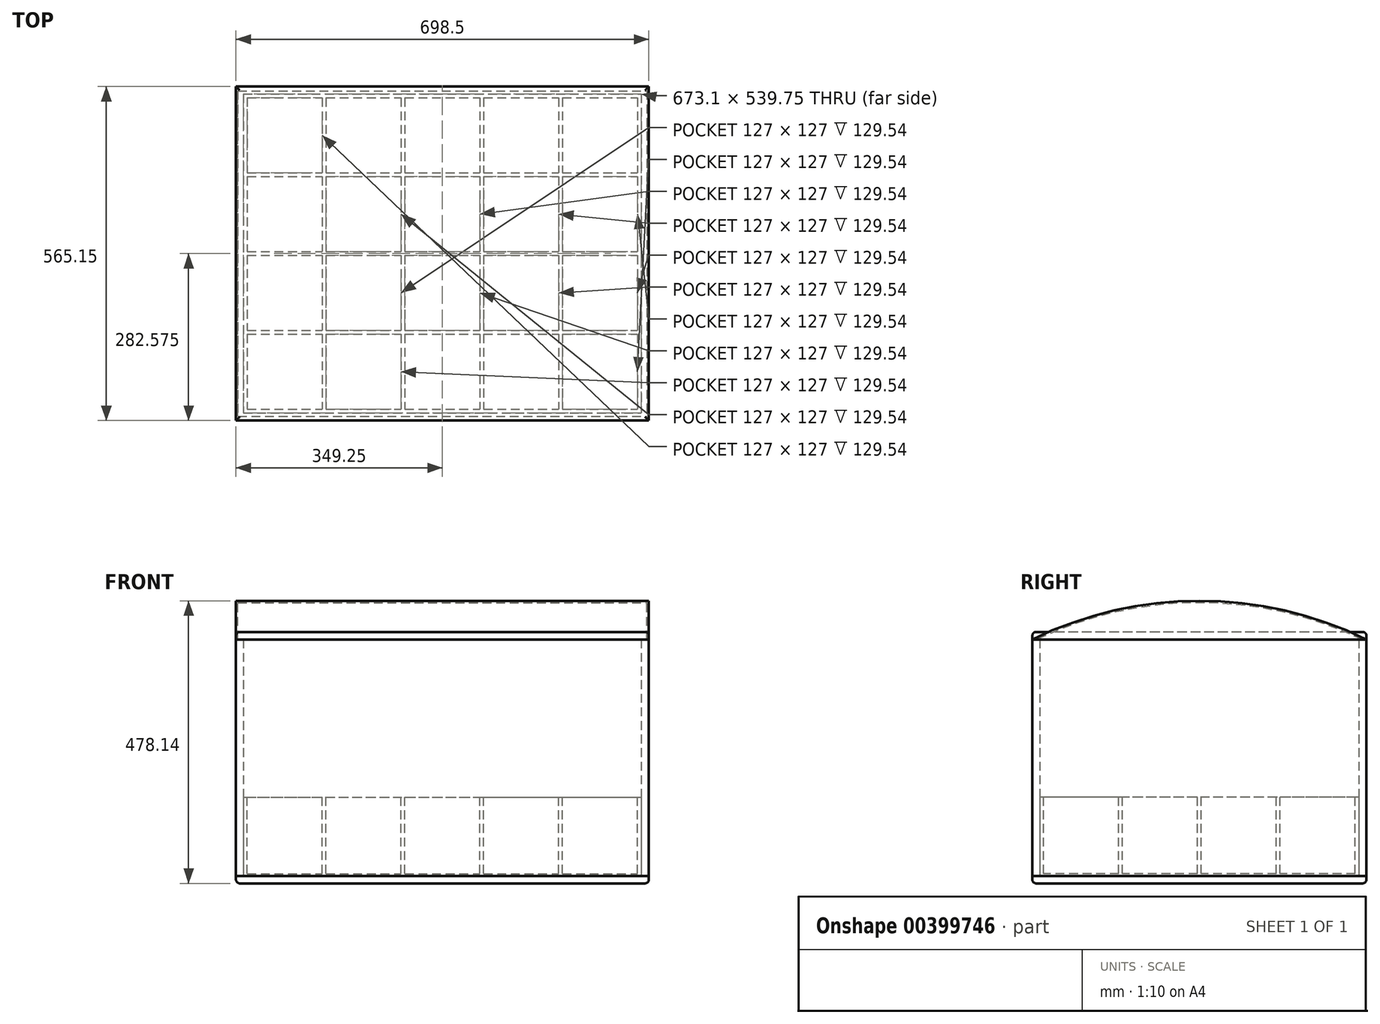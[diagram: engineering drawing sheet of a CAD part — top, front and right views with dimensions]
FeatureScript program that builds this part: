
annotation { "Feature Type Name" : "Feature", "Feature Type Description" : "" }
export const myFeature = defineFeature(function(context is Context, id is Id, definition is map)
    precondition{}
    {
        {
            var Q0;
            Q0=qCreatedBy(makeId("Top.planeOp"),FACE);
            var sketch = newSketch(context, id + "F0", { "sketchPlane" : qUnion([Q0])});
            skLineSegment(sketch, "E0.bottom", {"start": v(0, 0) * mm, "end": v(673.1, 0) * mm, "construction": true});
            skLineSegment(sketch, "E0.top", {"start": v(0, -539.75) * mm, "end": v(673.1, -539.75) * mm, "construction": true});
            skLineSegment(sketch, "E0.left", {"start": v(0, 0) * mm, "end": v(0, -539.75) * mm, "construction": true});
            skLineSegment(sketch, "E0.right", {"start": v(673.1, 0) * mm, "end": v(673.1, -539.75) * mm, "construction": true});
            skLineSegment(sketch, "E1.bottom", {"start": v(6.35, -6.35) * mm, "end": v(133.35, -6.35) * mm, "construction": true});
            skLineSegment(sketch, "E1.top", {"start": v(6.35, -133.35) * mm, "end": v(133.35, -133.35) * mm, "construction": true});
            skLineSegment(sketch, "E1.left", {"start": v(6.35, -6.35) * mm, "end": v(6.35, -133.35) * mm, "construction": true});
            skLineSegment(sketch, "E1.right", {"start": v(133.35, -6.35) * mm, "end": v(133.35, -133.35) * mm, "construction": true});
            skLineSegment(sketch, "E2.0.1.0", {"start": v(133.35, -139.7) * mm, "end": v(133.35, -266.7) * mm, "construction": true});
            skLineSegment(sketch, "E2.0.1.1", {"start": v(6.35, -139.7) * mm, "end": v(6.35, -266.7) * mm, "construction": true});
            skLineSegment(sketch, "E2.0.1.2", {"start": v(6.35, -266.7) * mm, "end": v(133.35, -266.7) * mm, "construction": true});
            skLineSegment(sketch, "E2.0.1.3", {"start": v(6.35, -139.7) * mm, "end": v(133.35, -139.7) * mm, "construction": true});
            skLineSegment(sketch, "E2.0.2.0", {"start": v(133.35, -273.05) * mm, "end": v(133.35, -400.05) * mm, "construction": true});
            skLineSegment(sketch, "E2.0.2.1", {"start": v(6.35, -273.05) * mm, "end": v(6.35, -400.05) * mm, "construction": true});
            skLineSegment(sketch, "E2.0.2.2", {"start": v(6.35, -400.05) * mm, "end": v(133.35, -400.05) * mm, "construction": true});
            skLineSegment(sketch, "E2.0.2.3", {"start": v(6.35, -273.05) * mm, "end": v(133.35, -273.05) * mm, "construction": true});
            skLineSegment(sketch, "E2.1.0.0", {"start": v(266.7, -6.35) * mm, "end": v(266.7, -133.35) * mm, "construction": true});
            skLineSegment(sketch, "E2.1.0.1", {"start": v(139.7, -6.35) * mm, "end": v(139.7, -133.35) * mm, "construction": true});
            skLineSegment(sketch, "E2.1.0.2", {"start": v(139.7, -133.35) * mm, "end": v(266.7, -133.35) * mm, "construction": true});
            skLineSegment(sketch, "E2.1.0.3", {"start": v(139.7, -6.35) * mm, "end": v(266.7, -6.35) * mm, "construction": true});
            skLineSegment(sketch, "E2.1.1.0", {"start": v(266.7, -139.7) * mm, "end": v(266.7, -266.7) * mm, "construction": true});
            skLineSegment(sketch, "E2.1.1.1", {"start": v(139.7, -139.7) * mm, "end": v(139.7, -266.7) * mm, "construction": true});
            skLineSegment(sketch, "E2.1.1.2", {"start": v(139.7, -266.7) * mm, "end": v(266.7, -266.7) * mm, "construction": true});
            skLineSegment(sketch, "E2.1.1.3", {"start": v(139.7, -139.7) * mm, "end": v(266.7, -139.7) * mm, "construction": true});
            skLineSegment(sketch, "E2.1.2.0", {"start": v(266.7, -273.05) * mm, "end": v(266.7, -400.05) * mm, "construction": true});
            skLineSegment(sketch, "E2.1.2.1", {"start": v(139.7, -273.05) * mm, "end": v(139.7, -400.05) * mm, "construction": true});
            skLineSegment(sketch, "E2.1.2.2", {"start": v(139.7, -400.05) * mm, "end": v(266.7, -400.05) * mm, "construction": true});
            skLineSegment(sketch, "E2.1.2.3", {"start": v(139.7, -273.05) * mm, "end": v(266.7, -273.05) * mm, "construction": true});
            skLineSegment(sketch, "E2.2.0.0", {"start": v(400.05, -6.35) * mm, "end": v(400.05, -133.35) * mm, "construction": true});
            skLineSegment(sketch, "E2.2.0.1", {"start": v(273.05, -6.35) * mm, "end": v(273.05, -133.35) * mm, "construction": true});
            skLineSegment(sketch, "E2.2.0.2", {"start": v(273.05, -133.35) * mm, "end": v(400.05, -133.35) * mm, "construction": true});
            skLineSegment(sketch, "E2.2.0.3", {"start": v(273.05, -6.35) * mm, "end": v(400.05, -6.35) * mm, "construction": true});
            skLineSegment(sketch, "E2.2.1.0", {"start": v(400.05, -139.7) * mm, "end": v(400.05, -266.7) * mm, "construction": true});
            skLineSegment(sketch, "E2.2.1.1", {"start": v(273.05, -139.7) * mm, "end": v(273.05, -266.7) * mm, "construction": true});
            skLineSegment(sketch, "E2.2.1.2", {"start": v(273.05, -266.7) * mm, "end": v(400.05, -266.7) * mm, "construction": true});
            skLineSegment(sketch, "E2.2.1.3", {"start": v(273.05, -139.7) * mm, "end": v(400.05, -139.7) * mm, "construction": true});
            skLineSegment(sketch, "E2.2.2.0", {"start": v(400.05, -273.05) * mm, "end": v(400.05, -400.05) * mm, "construction": true});
            skLineSegment(sketch, "E2.2.2.1", {"start": v(273.05, -273.05) * mm, "end": v(273.05, -400.05) * mm, "construction": true});
            skLineSegment(sketch, "E2.2.2.2", {"start": v(273.05, -400.05) * mm, "end": v(400.05, -400.05) * mm, "construction": true});
            skLineSegment(sketch, "E2.2.2.3", {"start": v(273.05, -273.05) * mm, "end": v(400.05, -273.05) * mm, "construction": true});
            skLineSegment(sketch, "E2.direction1", {"start": v(6.35, -133.35) * mm, "end": v(139.7, -133.35) * mm, "construction": true});
            skLineSegment(sketch, "E2.direction2", {"start": v(6.35, -133.35) * mm, "end": v(6.35, -266.7) * mm, "construction": true});
            skLineSegment(sketch, "E3.0.3.0", {"start": v(533.4, -6.35) * mm, "end": v(533.4, -133.35) * mm, "construction": true});
            skLineSegment(sketch, "E3.3.3.0", {"start": v(406.4, -6.35) * mm, "end": v(406.4, -133.35) * mm, "construction": true});
            skLineSegment(sketch, "E3.6.3.0", {"start": v(406.4, -133.35) * mm, "end": v(533.4, -133.35) * mm, "construction": true});
            skLineSegment(sketch, "E3.9.3.0", {"start": v(406.4, -6.35) * mm, "end": v(533.4, -6.35) * mm, "construction": true});
            skLineSegment(sketch, "E3.0.3.1", {"start": v(533.4, -139.7) * mm, "end": v(533.4, -266.7) * mm, "construction": true});
            skLineSegment(sketch, "E3.3.3.1", {"start": v(406.4, -139.7) * mm, "end": v(406.4, -266.7) * mm, "construction": true});
            skLineSegment(sketch, "E3.6.3.1", {"start": v(406.4, -266.7) * mm, "end": v(533.4, -266.7) * mm, "construction": true});
            skLineSegment(sketch, "E3.9.3.1", {"start": v(406.4, -139.7) * mm, "end": v(533.4, -139.7) * mm, "construction": true});
            skLineSegment(sketch, "E3.0.3.2", {"start": v(533.4, -273.05) * mm, "end": v(533.4, -400.05) * mm, "construction": true});
            skLineSegment(sketch, "E3.3.3.2", {"start": v(406.4, -273.05) * mm, "end": v(406.4, -400.05) * mm, "construction": true});
            skLineSegment(sketch, "E3.6.3.2", {"start": v(406.4, -400.05) * mm, "end": v(533.4, -400.05) * mm, "construction": true});
            skLineSegment(sketch, "E3.9.3.2", {"start": v(406.4, -273.05) * mm, "end": v(533.4, -273.05) * mm, "construction": true});
            skLineSegment(sketch, "E4.0.0.3", {"start": v(133.35, -406.4) * mm, "end": v(133.35, -533.4) * mm, "construction": true});
            skLineSegment(sketch, "E4.3.0.3", {"start": v(6.35, -406.4) * mm, "end": v(6.35, -533.4) * mm, "construction": true});
            skLineSegment(sketch, "E4.6.0.3", {"start": v(6.35, -533.4) * mm, "end": v(133.35, -533.4) * mm, "construction": true});
            skLineSegment(sketch, "E4.9.0.3", {"start": v(6.35, -406.4) * mm, "end": v(133.35, -406.4) * mm, "construction": true});
            skLineSegment(sketch, "E4.0.1.3", {"start": v(266.7, -406.4) * mm, "end": v(266.7, -533.4) * mm, "construction": true});
            skLineSegment(sketch, "E4.3.1.3", {"start": v(139.7, -406.4) * mm, "end": v(139.7, -533.4) * mm, "construction": true});
            skLineSegment(sketch, "E4.6.1.3", {"start": v(139.7, -533.4) * mm, "end": v(266.7, -533.4) * mm, "construction": true});
            skLineSegment(sketch, "E4.9.1.3", {"start": v(139.7, -406.4) * mm, "end": v(266.7, -406.4) * mm, "construction": true});
            skLineSegment(sketch, "E4.0.2.3", {"start": v(400.05, -406.4) * mm, "end": v(400.05, -533.4) * mm, "construction": true});
            skLineSegment(sketch, "E4.3.2.3", {"start": v(273.05, -406.4) * mm, "end": v(273.05, -533.4) * mm, "construction": true});
            skLineSegment(sketch, "E4.6.2.3", {"start": v(273.05, -533.4) * mm, "end": v(400.05, -533.4) * mm, "construction": true});
            skLineSegment(sketch, "E4.9.2.3", {"start": v(273.05, -406.4) * mm, "end": v(400.05, -406.4) * mm, "construction": true});
            skLineSegment(sketch, "E4.0.3.3", {"start": v(533.4, -406.4) * mm, "end": v(533.4, -533.4) * mm, "construction": true});
            skLineSegment(sketch, "E4.3.3.3", {"start": v(406.4, -406.4) * mm, "end": v(406.4, -533.4) * mm, "construction": true});
            skLineSegment(sketch, "E4.6.3.3", {"start": v(406.4, -533.4) * mm, "end": v(533.4, -533.4) * mm, "construction": true});
            skLineSegment(sketch, "E4.9.3.3", {"start": v(406.4, -406.4) * mm, "end": v(533.4, -406.4) * mm, "construction": true});
            skLineSegment(sketch, "E5.0.4.0", {"start": v(666.75, -6.35) * mm, "end": v(666.75, -133.35) * mm, "construction": true});
            skLineSegment(sketch, "E5.3.4.0", {"start": v(539.75, -6.35) * mm, "end": v(539.75, -133.35) * mm, "construction": true});
            skLineSegment(sketch, "E5.6.4.0", {"start": v(539.75, -133.35) * mm, "end": v(666.75, -133.35) * mm, "construction": true});
            skLineSegment(sketch, "E5.9.4.0", {"start": v(539.75, -6.35) * mm, "end": v(666.75, -6.35) * mm, "construction": true});
            skLineSegment(sketch, "E5.0.4.1", {"start": v(666.75, -139.7) * mm, "end": v(666.75, -266.7) * mm, "construction": true});
            skLineSegment(sketch, "E5.3.4.1", {"start": v(539.75, -139.7) * mm, "end": v(539.75, -266.7) * mm, "construction": true});
            skLineSegment(sketch, "E5.6.4.1", {"start": v(539.75, -266.7) * mm, "end": v(666.75, -266.7) * mm, "construction": true});
            skLineSegment(sketch, "E5.9.4.1", {"start": v(539.75, -139.7) * mm, "end": v(666.75, -139.7) * mm, "construction": true});
            skLineSegment(sketch, "E5.0.4.2", {"start": v(666.75, -273.05) * mm, "end": v(666.75, -400.05) * mm, "construction": true});
            skLineSegment(sketch, "E5.3.4.2", {"start": v(539.75, -273.05) * mm, "end": v(539.75, -400.05) * mm, "construction": true});
            skLineSegment(sketch, "E5.6.4.2", {"start": v(539.75, -400.05) * mm, "end": v(666.75, -400.05) * mm, "construction": true});
            skLineSegment(sketch, "E5.9.4.2", {"start": v(539.75, -273.05) * mm, "end": v(666.75, -273.05) * mm, "construction": true});
            skLineSegment(sketch, "E5.0.4.3", {"start": v(666.75, -406.4) * mm, "end": v(666.75, -533.4) * mm, "construction": true});
            skLineSegment(sketch, "E5.3.4.3", {"start": v(539.75, -406.4) * mm, "end": v(539.75, -533.4) * mm, "construction": true});
            skLineSegment(sketch, "E5.6.4.3", {"start": v(539.75, -533.4) * mm, "end": v(666.75, -533.4) * mm, "construction": true});
            skLineSegment(sketch, "E5.9.4.3", {"start": v(539.75, -406.4) * mm, "end": v(666.75, -406.4) * mm, "construction": true});
            skSolve(sketch);
        }
        {
            var Q0;
            Q0=qCreatedBy(makeId("Top.planeOp"),FACE);
            var sketch = newSketch(context, id + "F1", { "sketchPlane" : qUnion([Q0])});
            skLineSegment(sketch, "E6.0", {"start": v(0, 0) * mm, "end": v(673.1, 0) * mm});
            skLineSegment(sketch, "E7.0", {"start": v(673.1, 0) * mm, "end": v(673.1, -539.75) * mm});
            skLineSegment(sketch, "E8.0", {"start": v(0, -539.75) * mm, "end": v(673.1, -539.75) * mm});
            skLineSegment(sketch, "E9.0", {"start": v(0, 0) * mm, "end": v(0, -539.75) * mm});
            skSolve(sketch);
        }
        {
            var Q0;
            Q0 = qSketchRegion(id + "F1", true);
            extrude(context, id + "F2", {"entities" : qUnion([Q0]), "depth" : 133.35 * mm});
        }
        {
            var Q0;
            Q0=makeQuery(id+"F2.opExtrude","CAP_FACE",FACE,{"disambiguationData":[OSD([sQuery(id+"F1.wireOp",EDGE,"E6.0"),sQuery(id+"F1.wireOp",EDGE,"E7.0"),sQuery(id+"F1.wireOp",EDGE,"E8.0"),sQuery(id+"F1.wireOp",EDGE,"E9.0")])],"isStart":false});
            var sketch = newSketch(context, id + "F3", { "sketchPlane" : qUnion([Q0])});
            skLineSegment(sketch, "E10.0", {"start": v(6.35, -266.7) * mm, "end": v(133.35, -266.7) * mm});
            skLineSegment(sketch, "E10.1", {"start": v(273.05, -139.7) * mm, "end": v(400.05, -139.7) * mm});
            skLineSegment(sketch, "E10.2", {"start": v(539.75, -533.4) * mm, "end": v(666.75, -533.4) * mm});
            skLineSegment(sketch, "E10.3", {"start": v(139.7, -273.05) * mm, "end": v(139.7, -400.05) * mm});
            skLineSegment(sketch, "E10.4", {"start": v(6.35, -533.4) * mm, "end": v(133.35, -533.4) * mm});
            skLineSegment(sketch, "E10.5", {"start": v(6.35, -406.4) * mm, "end": v(6.35, -533.4) * mm});
            skLineSegment(sketch, "E10.6", {"start": v(133.35, -273.05) * mm, "end": v(133.35, -400.05) * mm});
            skLineSegment(sketch, "E10.7", {"start": v(273.05, -133.35) * mm, "end": v(400.05, -133.35) * mm});
            skLineSegment(sketch, "E10.8", {"start": v(139.7, -6.35) * mm, "end": v(266.7, -6.35) * mm});
            skLineSegment(sketch, "E10.9", {"start": v(0, 0) * mm, "end": v(0, -539.75) * mm});
            skLineSegment(sketch, "E10.10", {"start": v(539.75, -6.35) * mm, "end": v(666.75, -6.35) * mm});
            skLineSegment(sketch, "E10.11", {"start": v(539.75, -139.7) * mm, "end": v(666.75, -139.7) * mm});
            skLineSegment(sketch, "E10.12", {"start": v(406.4, -273.05) * mm, "end": v(406.4, -400.05) * mm});
            skLineSegment(sketch, "E10.13", {"start": v(539.75, -273.05) * mm, "end": v(539.75, -400.05) * mm});
            skLineSegment(sketch, "E10.14", {"start": v(533.4, -139.7) * mm, "end": v(533.4, -266.7) * mm});
            skLineSegment(sketch, "E10.15", {"start": v(273.05, -273.05) * mm, "end": v(273.05, -400.05) * mm});
            skLineSegment(sketch, "E10.16", {"start": v(539.75, -266.7) * mm, "end": v(666.75, -266.7) * mm});
            skLineSegment(sketch, "E10.17", {"start": v(666.75, -273.05) * mm, "end": v(666.75, -400.05) * mm});
            skLineSegment(sketch, "E10.18", {"start": v(133.35, -406.4) * mm, "end": v(133.35, -533.4) * mm});
            skLineSegment(sketch, "E10.19", {"start": v(539.75, -406.4) * mm, "end": v(666.75, -406.4) * mm});
            skLineSegment(sketch, "E10.20", {"start": v(139.7, -406.4) * mm, "end": v(139.7, -533.4) * mm});
            skLineSegment(sketch, "E10.21", {"start": v(539.75, -133.35) * mm, "end": v(666.75, -133.35) * mm});
            skLineSegment(sketch, "E10.22", {"start": v(266.7, -139.7) * mm, "end": v(266.7, -266.7) * mm});
            skLineSegment(sketch, "E10.23", {"start": v(6.35, -273.05) * mm, "end": v(6.35, -400.05) * mm});
            skLineSegment(sketch, "E10.24", {"start": v(139.7, -273.05) * mm, "end": v(266.7, -273.05) * mm});
            skLineSegment(sketch, "E10.25", {"start": v(139.7, -406.4) * mm, "end": v(266.7, -406.4) * mm});
            skLineSegment(sketch, "E10.26", {"start": v(6.35, -6.35) * mm, "end": v(6.35, -133.35) * mm});
            skLineSegment(sketch, "E10.27", {"start": v(666.75, -139.7) * mm, "end": v(666.75, -266.7) * mm});
            skLineSegment(sketch, "E10.28", {"start": v(400.05, -406.4) * mm, "end": v(400.05, -533.4) * mm});
            skLineSegment(sketch, "E10.29", {"start": v(673.1, 0) * mm, "end": v(673.1, -539.75) * mm});
            skLineSegment(sketch, "E10.30", {"start": v(406.4, -533.4) * mm, "end": v(533.4, -533.4) * mm});
            skLineSegment(sketch, "E10.31", {"start": v(133.35, -6.35) * mm, "end": v(133.35, -133.35) * mm});
            skLineSegment(sketch, "E10.32", {"start": v(6.35, -139.7) * mm, "end": v(133.35, -139.7) * mm});
            skLineSegment(sketch, "E10.33", {"start": v(133.35, -139.7) * mm, "end": v(133.35, -266.7) * mm});
            skLineSegment(sketch, "E10.34", {"start": v(6.35, -6.35) * mm, "end": v(133.35, -6.35) * mm});
            skLineSegment(sketch, "E10.35", {"start": v(6.35, -400.05) * mm, "end": v(133.35, -400.05) * mm});
            skLineSegment(sketch, "E10.36", {"start": v(139.7, -139.7) * mm, "end": v(139.7, -266.7) * mm});
            skLineSegment(sketch, "E10.37", {"start": v(539.75, -406.4) * mm, "end": v(539.75, -533.4) * mm});
            skLineSegment(sketch, "E10.38", {"start": v(6.35, -273.05) * mm, "end": v(133.35, -273.05) * mm});
            skLineSegment(sketch, "E10.39", {"start": v(406.4, -6.35) * mm, "end": v(406.4, -133.35) * mm});
            skLineSegment(sketch, "E10.40", {"start": v(406.4, -273.05) * mm, "end": v(533.4, -273.05) * mm});
            skLineSegment(sketch, "E10.41", {"start": v(406.4, -139.7) * mm, "end": v(406.4, -266.7) * mm});
            skLineSegment(sketch, "E10.42", {"start": v(666.75, -6.35) * mm, "end": v(666.75, -133.35) * mm});
            skLineSegment(sketch, "E10.43", {"start": v(533.4, -6.35) * mm, "end": v(533.4, -133.35) * mm});
            skLineSegment(sketch, "E10.44", {"start": v(273.05, -533.4) * mm, "end": v(400.05, -533.4) * mm});
            skLineSegment(sketch, "E10.45", {"start": v(0, -539.75) * mm, "end": v(673.1, -539.75) * mm});
            skLineSegment(sketch, "E10.46", {"start": v(273.05, -400.05) * mm, "end": v(400.05, -400.05) * mm});
            skLineSegment(sketch, "E10.47", {"start": v(273.05, -406.4) * mm, "end": v(273.05, -533.4) * mm});
            skLineSegment(sketch, "E10.48", {"start": v(406.4, -400.05) * mm, "end": v(533.4, -400.05) * mm});
            skLineSegment(sketch, "E10.49", {"start": v(139.7, -266.7) * mm, "end": v(266.7, -266.7) * mm});
            skLineSegment(sketch, "E10.50", {"start": v(6.35, -139.7) * mm, "end": v(6.35, -266.7) * mm});
            skLineSegment(sketch, "E10.51", {"start": v(266.7, -273.05) * mm, "end": v(266.7, -400.05) * mm});
            skLineSegment(sketch, "E10.52", {"start": v(406.4, -266.7) * mm, "end": v(533.4, -266.7) * mm});
            skLineSegment(sketch, "E10.53", {"start": v(273.05, -6.35) * mm, "end": v(400.05, -6.35) * mm});
            skLineSegment(sketch, "E10.54", {"start": v(139.7, -139.7) * mm, "end": v(266.7, -139.7) * mm});
            skLineSegment(sketch, "E10.55", {"start": v(273.05, -273.05) * mm, "end": v(400.05, -273.05) * mm});
            skLineSegment(sketch, "E10.56", {"start": v(6.35, -133.35) * mm, "end": v(133.35, -133.35) * mm});
            skLineSegment(sketch, "E10.57", {"start": v(139.7, -400.05) * mm, "end": v(266.7, -400.05) * mm});
            skLineSegment(sketch, "E10.58", {"start": v(539.75, -400.05) * mm, "end": v(666.75, -400.05) * mm});
            skLineSegment(sketch, "E10.59", {"start": v(139.7, -533.4) * mm, "end": v(266.7, -533.4) * mm});
            skLineSegment(sketch, "E10.60", {"start": v(539.75, -6.35) * mm, "end": v(539.75, -133.35) * mm});
            skLineSegment(sketch, "E10.61", {"start": v(273.05, -6.35) * mm, "end": v(273.05, -133.35) * mm});
            skLineSegment(sketch, "E10.62", {"start": v(400.05, -6.35) * mm, "end": v(400.05, -133.35) * mm});
            skLineSegment(sketch, "E10.63", {"start": v(406.4, -406.4) * mm, "end": v(533.4, -406.4) * mm});
            skLineSegment(sketch, "E10.64", {"start": v(406.4, -6.35) * mm, "end": v(533.4, -6.35) * mm});
            skLineSegment(sketch, "E10.65", {"start": v(400.05, -139.7) * mm, "end": v(400.05, -266.7) * mm});
            skLineSegment(sketch, "E10.66", {"start": v(406.4, -133.35) * mm, "end": v(533.4, -133.35) * mm});
            skLineSegment(sketch, "E10.67", {"start": v(266.7, -406.4) * mm, "end": v(266.7, -533.4) * mm});
            skLineSegment(sketch, "E10.68", {"start": v(539.75, -139.7) * mm, "end": v(539.75, -266.7) * mm});
            skLineSegment(sketch, "E10.69", {"start": v(400.05, -273.05) * mm, "end": v(400.05, -400.05) * mm});
            skLineSegment(sketch, "E10.70", {"start": v(266.7, -6.35) * mm, "end": v(266.7, -133.35) * mm});
            skLineSegment(sketch, "E10.71", {"start": v(406.4, -406.4) * mm, "end": v(406.4, -533.4) * mm});
            skLineSegment(sketch, "E10.72", {"start": v(6.35, -406.4) * mm, "end": v(133.35, -406.4) * mm});
            skLineSegment(sketch, "E10.73", {"start": v(139.7, -6.35) * mm, "end": v(139.7, -133.35) * mm});
            skLineSegment(sketch, "E10.74", {"start": v(539.75, -273.05) * mm, "end": v(666.75, -273.05) * mm});
            skLineSegment(sketch, "E10.75", {"start": v(273.05, -406.4) * mm, "end": v(400.05, -406.4) * mm});
            skLineSegment(sketch, "E10.76", {"start": v(406.4, -139.7) * mm, "end": v(533.4, -139.7) * mm});
            skLineSegment(sketch, "E10.77", {"start": v(273.05, -139.7) * mm, "end": v(273.05, -266.7) * mm});
            skLineSegment(sketch, "E10.78", {"start": v(139.7, -133.35) * mm, "end": v(266.7, -133.35) * mm});
            skLineSegment(sketch, "E10.79", {"start": v(666.75, -406.4) * mm, "end": v(666.75, -533.4) * mm});
            skLineSegment(sketch, "E10.80", {"start": v(533.4, -406.4) * mm, "end": v(533.4, -533.4) * mm});
            skLineSegment(sketch, "E10.81", {"start": v(533.4, -273.05) * mm, "end": v(533.4, -400.05) * mm});
            skLineSegment(sketch, "E10.82", {"start": v(273.05, -266.7) * mm, "end": v(400.05, -266.7) * mm});
            skSolve(sketch);
        }
        {
            var Q0;
            Q0 = qSketchRegion(id + "F3", true);
            extrude(context, id + "F4", {"entities" : qUnion([Q0]), "operationType" : NewBodyOperationType.REMOVE, "oppositeDirection" : true, "depth" : 129.54 * mm});
        }
        {
            var Q0;
            Q0=makeQuery(id+"F2.opExtrude","CAP_FACE",FACE,{"disambiguationData":[OSD([sQuery(id+"F1.wireOp",EDGE,"E6.0"),sQuery(id+"F1.wireOp",EDGE,"E7.0"),sQuery(id+"F1.wireOp",EDGE,"E8.0"),sQuery(id+"F1.wireOp",EDGE,"E9.0")])],"isStart":true});
            var sketch = newSketch(context, id + "F5", { "sketchPlane" : qUnion([Q0])});
            skLineSegment(sketch, "E11.0", {"start": v(-12.7, 552.45) * mm, "end": v(685.8, 552.45) * mm});
            skLineSegment(sketch, "E11.1", {"start": v(-12.7, -12.7) * mm, "end": v(-12.7, 552.45) * mm});
            skLineSegment(sketch, "E11.2", {"start": v(-12.7, -12.7) * mm, "end": v(685.8, -12.7) * mm});
            skLineSegment(sketch, "E11.3", {"start": v(685.8, -12.7) * mm, "end": v(685.8, 552.45) * mm});
            skSolve(sketch);
        }
        {
            var Q0;
            Q0 = qSketchRegion(id + "F5", true);
            extrude(context, id + "F6", {"entities" : qUnion([Q0]), "depth" : 12.7 * mm});
        }
        {
            var Q0;
            Q0=makeQuery(id+"F6.opExtrude","CAP_FACE",FACE,{"disambiguationData":[OSD([sQuery(id+"F5.wireOp",EDGE,"E11.0"),sQuery(id+"F5.wireOp",EDGE,"E11.1"),sQuery(id+"F5.wireOp",EDGE,"E11.2"),sQuery(id+"F5.wireOp",EDGE,"E11.3")])],"isStart":true});
            var sketch = newSketch(context, id + "F7", { "sketchPlane" : qUnion([Q0])});
            skLineSegment(sketch, "E12.0", {"start": v(-12.7, 12.7) * mm, "end": v(685.8, 12.7) * mm});
            skLineSegment(sketch, "E13.0", {"start": v(685.8, 12.7) * mm, "end": v(685.8, -552.45) * mm});
            skLineSegment(sketch, "E14.0", {"start": v(-12.7, -552.45) * mm, "end": v(685.8, -552.45) * mm});
            skLineSegment(sketch, "E15.0", {"start": v(-12.7, 12.7) * mm, "end": v(-12.7, -552.45) * mm});
            skLineSegment(sketch, "E16.0", {"start": v(0, 0) * mm, "end": v(0, -539.75) * mm});
            skLineSegment(sketch, "E17.0", {"start": v(0, 0) * mm, "end": v(673.1, 0) * mm});
            skLineSegment(sketch, "E18.0", {"start": v(673.1, 0) * mm, "end": v(673.1, -539.75) * mm});
            skLineSegment(sketch, "E19.0", {"start": v(0, -539.75) * mm, "end": v(673.1, -539.75) * mm});
            skSolve(sketch);
        }
        {
            var Q0;
            Q0 = qSketchRegion(id + "F7", true);
            extrude(context, id + "F8", {"entities" : qUnion([Q0]), "depth" : 400.05 * mm});
        }
        {
            var Q0;
            Q0=makeQuery(id+"F8.opExtrude","CAP_FACE",FACE,{"disambiguationData":[OSD([sQuery(id+"F7.wireOp",EDGE,"E12.0"),sQuery(id+"F7.wireOp",EDGE,"E13.0"),sQuery(id+"F7.wireOp",EDGE,"E14.0"),sQuery(id+"F7.wireOp",EDGE,"E15.0"),sQuery(id+"F7.wireOp",EDGE,"E16.0"),sQuery(id+"F7.wireOp",EDGE,"E17.0"),sQuery(id+"F7.wireOp",EDGE,"E18.0"),sQuery(id+"F7.wireOp",EDGE,"E19.0")])],"isStart":false});
            var sketch = newSketch(context, id + "F9", { "sketchPlane" : qUnion([Q0])});
            skLineSegment(sketch, "E20.0", {"start": v(-12.7, 12.7) * mm, "end": v(685.8, 12.7) * mm});
            skLineSegment(sketch, "E21.0", {"start": v(-12.7, 12.7) * mm, "end": v(-12.7, -552.45) * mm});
            skLineSegment(sketch, "E22.0", {"start": v(685.8, 12.7) * mm, "end": v(685.8, -552.45) * mm});
            skLineSegment(sketch, "E23.0", {"start": v(-12.7, -552.45) * mm, "end": v(685.8, -552.45) * mm});
            skSolve(sketch);
        }
        {
            var Q0;
            Q0 = qSketchRegion(id + "F9", true);
            extrude(context, id + "F10", {"entities" : qUnion([Q0]), "depth" : 12.7 * mm});
        }
        {
            var Q0;
            Q0=makeQuery(id+"F8.boolean.opBoolean","MERGE",EDGE,{"derivedFrom":[makeQuery(id+"F6.opExtrude","SWEPT_EDGE",EDGE,{"disambiguationData":[OSD([sQuery(id+"F5.wireOp",EDGE,"E11.2"),sQuery(id+"F5.wireOp",EDGE,"E11.3")])]}),makeQuery(id+"F8.opExtrude","SWEPT_EDGE",EDGE,{"disambiguationData":[OSD([sQuery(id+"F7.wireOp",EDGE,"E12.0"),sQuery(id+"F7.wireOp",EDGE,"E13.0")])]})]});
            var Q1;
            Q1=makeQuery(id+"F6.opExtrude","CAP_EDGE",EDGE,{"disambiguationData":[OSD([sQuery(id+"F5.wireOp",EDGE,"E11.2")])],"isStart":false});
            var Q2;
            Q2=makeQuery(id+"F8.boolean.opBoolean","MERGE",EDGE,{"derivedFrom":[makeQuery(id+"F6.opExtrude","SWEPT_EDGE",EDGE,{"disambiguationData":[OSD([sQuery(id+"F5.wireOp",EDGE,"E11.1"),sQuery(id+"F5.wireOp",EDGE,"E11.2")])]}),makeQuery(id+"F8.opExtrude","SWEPT_EDGE",EDGE,{"disambiguationData":[OSD([sQuery(id+"F7.wireOp",EDGE,"E12.0"),sQuery(id+"F7.wireOp",EDGE,"E15.0")])]})]});
            var Q3;
            Q3=makeQuery(id+"F6.opExtrude","CAP_FACE",FACE,{"disambiguationData":[OSD([sQuery(id+"F5.wireOp",EDGE,"E11.0"),sQuery(id+"F5.wireOp",EDGE,"E11.1"),sQuery(id+"F5.wireOp",EDGE,"E11.2"),sQuery(id+"F5.wireOp",EDGE,"E11.3")])],"isStart":false});
            var Q4;
            Q4=makeQuery(id+"F8.boolean.opBoolean","MERGE",EDGE,{"derivedFrom":[makeQuery(id+"F6.opExtrude","SWEPT_EDGE",EDGE,{"disambiguationData":[OSD([sQuery(id+"F5.wireOp",EDGE,"E11.0"),sQuery(id+"F5.wireOp",EDGE,"E11.3")])]}),makeQuery(id+"F8.opExtrude","SWEPT_EDGE",EDGE,{"disambiguationData":[OSD([sQuery(id+"F7.wireOp",EDGE,"E13.0"),sQuery(id+"F7.wireOp",EDGE,"E14.0")])]})]});
            var Q5;
            Q5=makeQuery(id+"F8.boolean.opBoolean","MERGE",EDGE,{"derivedFrom":[makeQuery(id+"F6.opExtrude","SWEPT_EDGE",EDGE,{"disambiguationData":[OSD([sQuery(id+"F5.wireOp",EDGE,"E11.0"),sQuery(id+"F5.wireOp",EDGE,"E11.1")])]}),makeQuery(id+"F8.opExtrude","SWEPT_EDGE",EDGE,{"disambiguationData":[OSD([sQuery(id+"F7.wireOp",EDGE,"E14.0"),sQuery(id+"F7.wireOp",EDGE,"E15.0")])]})]});
            var Q6;
            Q6=makeQuery(id+"F10.opExtrude","CAP_FACE",FACE,{"disambiguationData":[OSD([sQuery(id+"F9.wireOp",EDGE,"E20.0"),sQuery(id+"F9.wireOp",EDGE,"E21.0"),sQuery(id+"F9.wireOp",EDGE,"E22.0"),sQuery(id+"F9.wireOp",EDGE,"E23.0")])],"isStart":false});
            fillet(context, id + "F11", {"entities" : qUnion([Q0, Q1, Q2, Q3, Q4, Q5, Q6]), "radius" : 6.35 * mm, "tangentPropagation" : true, "allowEdgeOverflow" : false});
        }
        {
            var Q0;
            Q0=makeQuery(id+"F8.opExtrude","SWEPT_FACE",FACE,{"disambiguationData":[OSD([sQuery(id+"F7.wireOp",EDGE,"E13.0")])]});
            var sketch = newSketch(context, id + "F12", { "sketchPlane" : qUnion([Q0])});
            skArc(sketch, "E24", {"start": v(12.7, 400.05) * mm, "mid": v(-269.88, 465.44) * mm, "end": v(-552.45, 400.05) * mm});
            skLineSegment(sketch, "E25", {"start": v(-552.45, 400.05) * mm, "end": v(12.7, 400.05) * mm});
            skPoint(sketch, "E26.0", {"position": v(-552.45, 400.05) * mm});
            skPoint(sketch, "E27.0", {"position": v(12.7, 400.05) * mm});
            skSolve(sketch);
        }
        {
            var Q0;
            Q0 = qSketchRegion(id + "F12", true);
            var Q1;
            Q1=makeQuery(id+"F8.opExtrude","SWEPT_FACE",FACE,{"disambiguationData":[OSD([sQuery(id+"F7.wireOp",EDGE,"E15.0")])]});
            extrude(context, id + "F13", {"entities" : qUnion([Q0]), "endBound" : BoundingType.UP_TO_SURFACE, "oppositeDirection" : true, "endBoundEntityFace" : qUnion([Q1]), "depth" : 25.4 * mm});
        }
        {
            var Q0;
            Q0=makeQuery(id+"F13.opExtrude","SWEPT_FACE",FACE,{"disambiguationData":[OSD([sQuery(id+"F12.wireOp",EDGE,"E25")])]});
            shell(context, id + "F14", {"entities" : qUnion([Q0]), "thickness" : 3.17 * mm});
        }
    });
